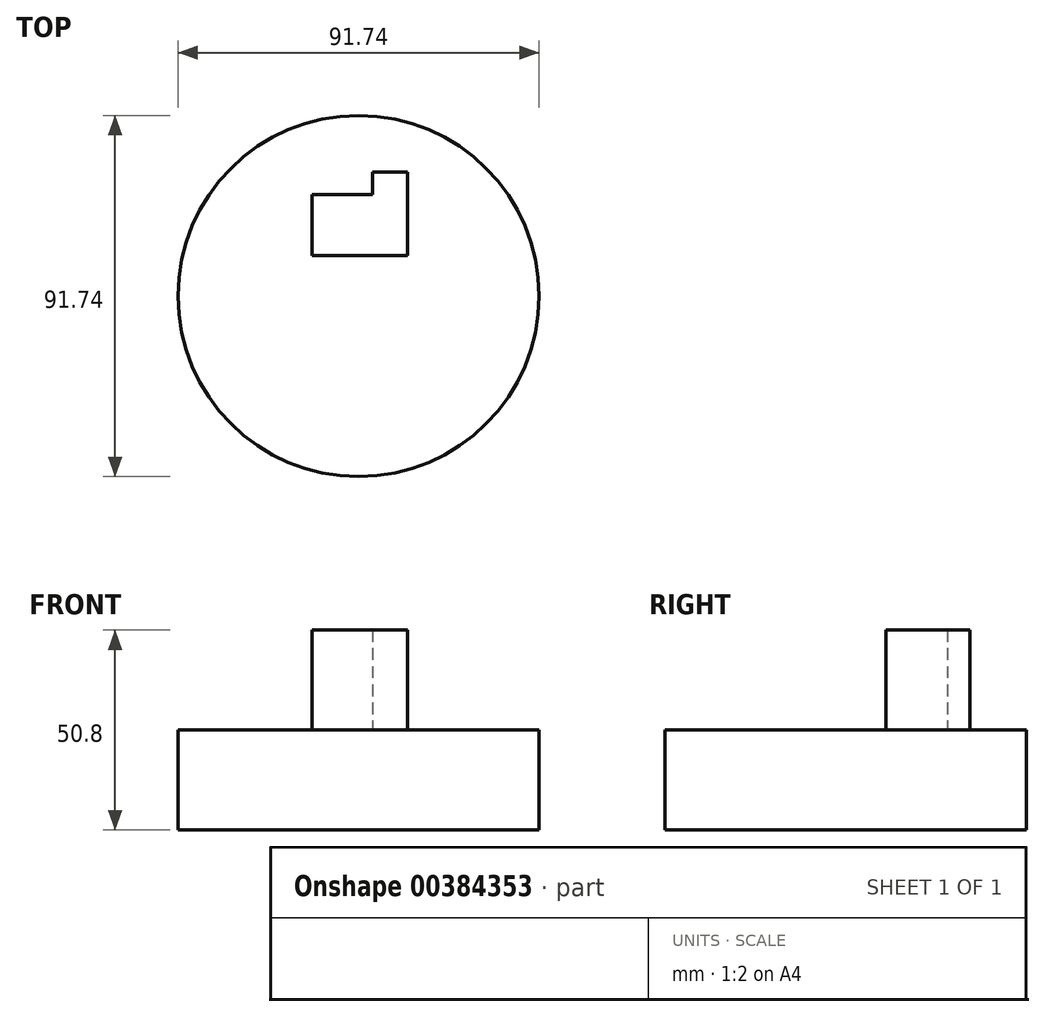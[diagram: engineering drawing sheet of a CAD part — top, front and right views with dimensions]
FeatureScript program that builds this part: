
annotation { "Feature Type Name" : "Feature", "Feature Type Description" : "" }
export const myFeature = defineFeature(function(context is Context, id is Id, definition is map)
    precondition{}
    {
        {
            var Q0;
            Q0=qCreatedBy(makeId("Top.planeOp"),FACE);
            var sketch = newSketch(context, id + "F0", { "sketchPlane" : qUnion([Q0])});
            skCircle(sketch, "E0", {"center": v(0, 0) * mm, "radius": 45.87 * mm});
            skSolve(sketch);
        }
        {
            var Q0;
            Q0 = qSketchRegion(id + "F0", true);
            extrude(context, id + "F1", {"entities" : qUnion([Q0]), "depth" : 25.4 * mm});
        }
        {
            var Q0;
            Q0=makeQuery(id+"F1.opExtrude","CAP_FACE",FACE,{"disambiguationData":[OSD([sQuery(id+"F0.wireOp",EDGE,"E0")])],"isStart":false});
            var sketch = newSketch(context, id + "F2", { "sketchPlane" : qUnion([Q0])});
            skLineSegment(sketch, "E1.bottom", {"start": v(-11.82, 25.82) * mm, "end": v(12.42, 25.82) * mm});
            skLineSegment(sketch, "E1.top", {"start": v(-11.82, 10.25) * mm, "end": v(12.42, 10.25) * mm});
            skLineSegment(sketch, "E1.left", {"start": v(-11.82, 25.82) * mm, "end": v(-11.82, 10.25) * mm});
            skLineSegment(sketch, "E1.right", {"start": v(12.42, 25.82) * mm, "end": v(12.42, 10.25) * mm});
            skLineSegment(sketch, "E2.bottom", {"start": v(3.55, 31.53) * mm, "end": v(12.42, 31.53) * mm});
            skLineSegment(sketch, "E2.top", {"start": v(3.55, 25.82) * mm, "end": v(12.42, 25.82) * mm});
            skLineSegment(sketch, "E2.left", {"start": v(3.55, 31.53) * mm, "end": v(3.55, 25.82) * mm});
            skLineSegment(sketch, "E2.right", {"start": v(12.42, 31.53) * mm, "end": v(12.42, 25.82) * mm});
            skSolve(sketch);
        }
        {
            var Q0;
            Q0 = qSketchRegion(id + "F2", true);
            extrude(context, id + "F3", {"entities" : qUnion([Q0]), "operationType" : NewBodyOperationType.ADD, "depth" : 25.4 * mm});
        }
    });
